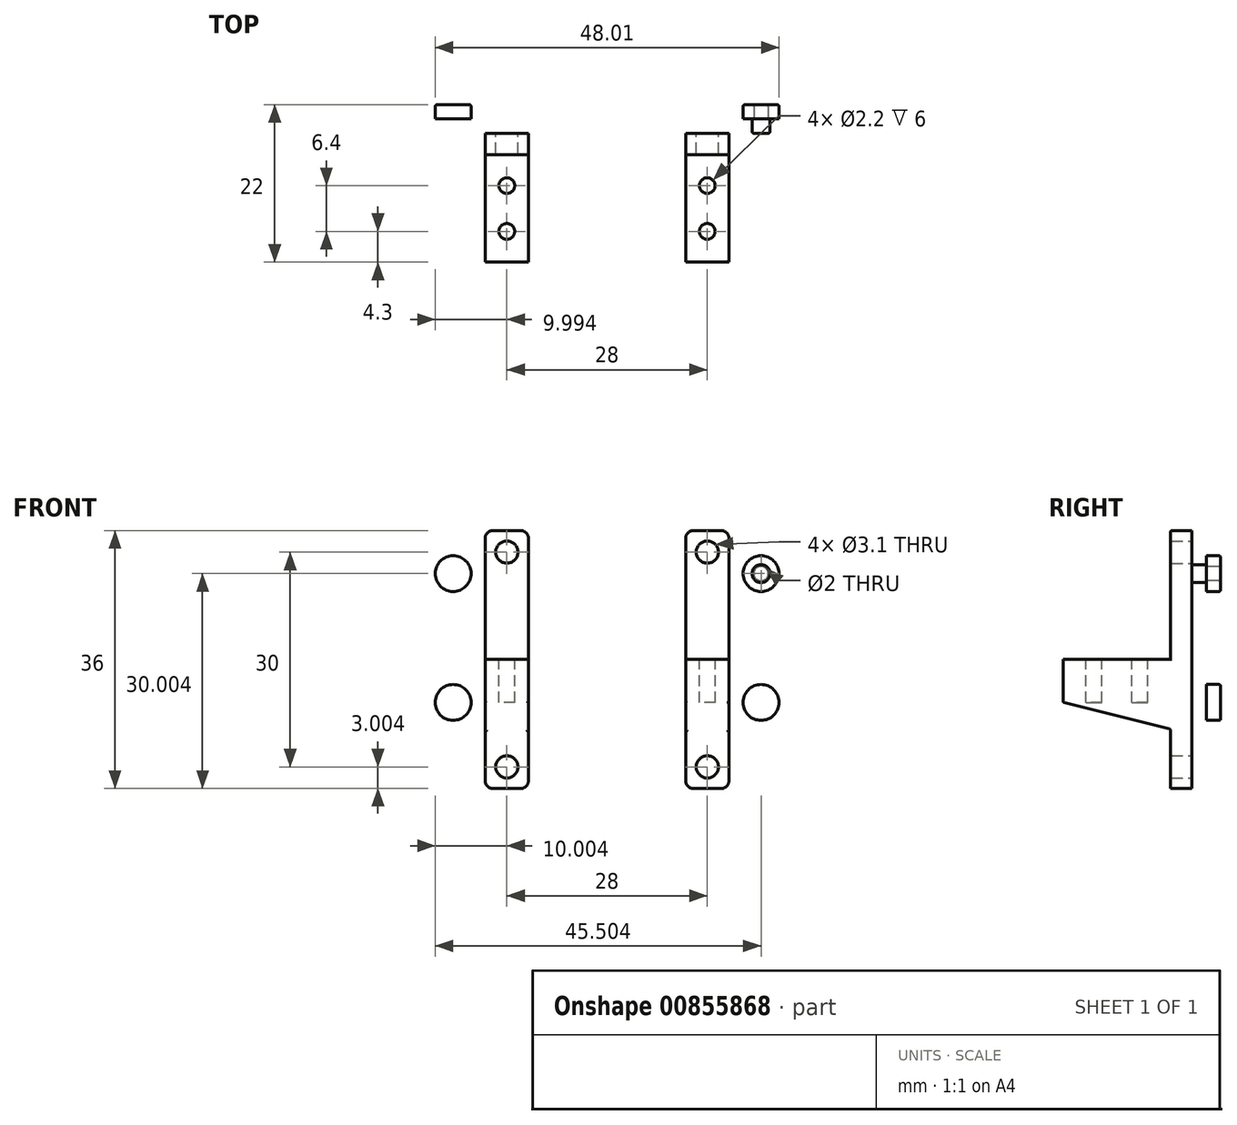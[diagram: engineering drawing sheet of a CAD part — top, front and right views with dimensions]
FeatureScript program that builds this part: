
annotation { "Feature Type Name" : "Feature", "Feature Type Description" : "" }
export const myFeature = defineFeature(function(context is Context, id is Id, definition is map)
    precondition{}
    {
        {
            var Q0;
            Q0=qCreatedBy(makeId("Front.planeOp"),FACE);
            var sketch = newSketch(context, id + "F0", { "sketchPlane" : qUnion([Q0])});
            skCircle(sketch, "E0", {"center": v(21.64, 10.68) * mm, "radius": 1.25 * mm});
            skCircle(sketch, "E1", {"center": v(21.64, -7.32) * mm, "radius": 1.25 * mm});
            skCircle(sketch, "E2", {"center": v(-21.36, 10.68) * mm, "radius": 1.25 * mm});
            skCircle(sketch, "E3", {"center": v(-21.36, -7.32) * mm, "radius": 1.25 * mm});
            skLineSegment(sketch, "E4", {"start": v(-12.6, 19.9) * mm, "end": v(12.89, 19.9) * mm});
            skLineSegment(sketch, "E5", {"start": v(-24.6, 10.6) * mm, "end": v(-24.6, -7.4) * mm});
            skLineSegment(sketch, "E6", {"start": v(24.9, 10.6) * mm, "end": v(24.9, -7.4) * mm});
            skLineSegment(sketch, "E7", {"start": v(14.2, -19.34) * mm, "end": v(-13.9, -19.34) * mm});
            skLineSegment(sketch, "E8", {"start": v(-15.36, -13.32) * mm, "end": v(-15.36, -16.32) * mm});
            skLineSegment(sketch, "E9", {"start": v(-12.36, -16.32) * mm, "end": v(-12.36, -13.32) * mm});
            skArc(sketch, "E10", {"start": v(-15.36, -16.32) * mm, "mid": v(-13.86, -17.82) * mm, "end": v(-12.36, -16.32) * mm});
            skArc(sketch, "E11", {"start": v(-12.36, -13.32) * mm, "mid": v(-13.86, -11.82) * mm, "end": v(-15.36, -13.32) * mm});
            skLineSegment(sketch, "E12", {"start": v(-15.36, 16.68) * mm, "end": v(-15.36, 13.68) * mm});
            skLineSegment(sketch, "E13", {"start": v(-12.36, 13.68) * mm, "end": v(-12.36, 16.68) * mm});
            skArc(sketch, "E14", {"start": v(-15.36, 13.68) * mm, "mid": v(-13.86, 12.18) * mm, "end": v(-12.36, 13.68) * mm});
            skArc(sketch, "E15", {"start": v(-12.36, 16.68) * mm, "mid": v(-13.86, 18.18) * mm, "end": v(-15.36, 16.68) * mm});
            skLineSegment(sketch, "E16", {"start": v(12.64, 16.68) * mm, "end": v(12.64, 13.68) * mm});
            skLineSegment(sketch, "E17", {"start": v(15.64, 13.68) * mm, "end": v(15.64, 16.68) * mm});
            skArc(sketch, "E18", {"start": v(12.64, 13.68) * mm, "mid": v(14.14, 12.18) * mm, "end": v(15.64, 13.68) * mm});
            skArc(sketch, "E19", {"start": v(15.64, 16.68) * mm, "mid": v(14.14, 18.18) * mm, "end": v(12.64, 16.68) * mm});
            skLineSegment(sketch, "E20", {"start": v(12.64, -13.32) * mm, "end": v(12.64, -16.32) * mm});
            skLineSegment(sketch, "E21", {"start": v(15.64, -16.32) * mm, "end": v(15.64, -13.32) * mm});
            skArc(sketch, "E22", {"start": v(12.64, -16.32) * mm, "mid": v(14.14, -17.82) * mm, "end": v(15.64, -16.32) * mm});
            skArc(sketch, "E23", {"start": v(15.64, -13.32) * mm, "mid": v(14.14, -11.82) * mm, "end": v(12.64, -13.32) * mm});
            skLineSegment(sketch, "E24", {"start": v(-9.86, 7.68) * mm, "end": v(-9.86, -7.32) * mm});
            skLineSegment(sketch, "E25", {"start": v(-6.86, -10.32) * mm, "end": v(7.14, -10.32) * mm});
            skLineSegment(sketch, "E26", {"start": v(10.14, -7.32) * mm, "end": v(10.14, 7.68) * mm});
            skLineSegment(sketch, "E27", {"start": v(7.14, 10.68) * mm, "end": v(-6.86, 10.68) * mm});
            skArc(sketch, "E28.filletArc", {"start": v(-6.86, 10.68) * mm, "mid": v(-8.98, 9.8) * mm, "end": v(-9.86, 7.68) * mm});
            skArc(sketch, "E29.filletArc", {"start": v(10.14, 7.68) * mm, "mid": v(9.26, 9.8) * mm, "end": v(7.14, 10.68) * mm});
            skArc(sketch, "E30.filletArc", {"start": v(7.14, -10.32) * mm, "mid": v(9.26, -9.44) * mm, "end": v(10.14, -7.32) * mm});
            skArc(sketch, "E31.filletArc", {"start": v(-9.86, -7.32) * mm, "mid": v(-8.98, -9.44) * mm, "end": v(-6.86, -10.32) * mm});
            skArc(sketch, "E32.filletArc", {"start": v(-12.6, 19.9) * mm, "mid": v(-14.56, 19.57) * mm, "end": v(-16.31, 18.61) * mm});
            skArc(sketch, "E33.filletArc", {"start": v(16.6, 18.61) * mm, "mid": v(14.85, 19.57) * mm, "end": v(12.89, 19.9) * mm});
            skLineSegment(sketch, "E34", {"start": v(23.76, -10.56) * mm, "end": v(18.06, -17.5) * mm});
            skLineSegment(sketch, "E35", {"start": v(22.57, 14.83) * mm, "end": v(16.6, 18.61) * mm});
            skLineSegment(sketch, "E36", {"start": v(-23.47, -10.56) * mm, "end": v(-17.77, -17.5) * mm});
            skLineSegment(sketch, "E37", {"start": v(-22.28, 14.83) * mm, "end": v(-16.31, 18.61) * mm});
            skArc(sketch, "E38.filletArc", {"start": v(-22.28, 14.83) * mm, "mid": v(-23.99, 13.02) * mm, "end": v(-24.6, 10.6) * mm});
            skArc(sketch, "E39.filletArc", {"start": v(-24.6, -7.4) * mm, "mid": v(-24.31, -9.08) * mm, "end": v(-23.47, -10.56) * mm});
            skArc(sketch, "E40.filletArc", {"start": v(23.76, -10.56) * mm, "mid": v(24.6, -9.08) * mm, "end": v(24.9, -7.4) * mm});
            skArc(sketch, "E41.filletArc", {"start": v(24.9, 10.6) * mm, "mid": v(24.27, 13.02) * mm, "end": v(22.57, 14.83) * mm});
            skArc(sketch, "E42.filletArc", {"start": v(-17.77, -17.5) * mm, "mid": v(-16.04, -18.86) * mm, "end": v(-13.9, -19.34) * mm});
            skArc(sketch, "E43.filletArc", {"start": v(14.2, -19.34) * mm, "mid": v(16.33, -18.86) * mm, "end": v(18.06, -17.5) * mm});
            skSolve(sketch);
        }
        {
            var Q0;
            Q0=makeQuery(id+"F0.imprint","IMPRINT",FACE,{"disambiguationData":[TD([[makeQuery(id+"F0.imprint","IMPRINT",EDGE,{"derivedFrom":sQuery(id+"F0.wireOp",EDGE,"E0")}),1.0]])]});
            extrude(context, id + "F1", {"entities" : qUnion([Q0]), "endBound" : BoundingType.SYMMETRIC, "offsetDistance" : 25 * mm, "depth" : 2 * mm});
        }
        {
            var Q0;
            Q0=makeQuery(id+"F1.opExtrude","CAP_FACE",FACE,{"disambiguationData":[OSD([sQuery(id+"F0.wireOp",EDGE,"b1f0e1de-7193-468a-b55f-a6da741b84d3"),sQuery(id+"F0.wireOp",EDGE,"6537f49a-e45f-4989-940a-a7038c38fff4"),sQuery(id+"F0.wireOp",EDGE,"8788dc07-e2e4-47d1-917b-d93742f93994"),sQuery(id+"F0.wireOp",EDGE,"47e42d19-3951-40ac-b4fd-01fcafdaa09f"),sQuery(id+"F0.wireOp",EDGE,"50e5991a-f910-4297-a0f5-58b0cc2bc1d4"),sQuery(id+"F0.wireOp",EDGE,"833c6bdf-bbd0-4c9a-a248-ca72598f08ba"),sQuery(id+"F0.wireOp",EDGE,"bd7a1b35-b3c5-4d82-882c-69e7568a474c"),sQuery(id+"F0.wireOp",EDGE,"ed142891-9665-4ff3-9cbf-df6a8f694267"),sQuery(id+"F0.wireOp",EDGE,"23a40c6b-513f-4e2b-90a4-2960991b2cb5"),sQuery(id+"F0.wireOp",EDGE,"b176ce0e-36f0-4206-846a-287cc205a3f0"),sQuery(id+"F0.wireOp",EDGE,"fd2f453c-b56c-4dc5-826e-d680bcd9d531"),sQuery(id+"F0.wireOp",EDGE,"4c904b9e-ebe1-46e0-9133-f6789165a817"),sQuery(id+"F0.wireOp",EDGE,"7d301a29-2a78-4614-95a1-4e57b7e65221"),sQuery(id+"F0.wireOp",EDGE,"bb945b4e-dbfa-4606-a6d0-c193b2a083f5"),sQuery(id+"F0.wireOp",EDGE,"f4a1adec-4f2b-4cc0-960b-66cac54fa532"),sQuery(id+"F0.wireOp",EDGE,"62c7bd33-5918-4929-8abe-04f5cd03c51a"),sQuery(id+"F0.wireOp",EDGE,"ff2f2cbf-8293-4aa6-ab80-3f50b4d68cad"),sQuery(id+"F0.wireOp",EDGE,"c173fb08-37eb-45d5-abb3-169ab915dbf1"),sQuery(id+"F0.wireOp",EDGE,"3b8e2cb5-3b84-4c06-aae3-f4915deb625e"),sQuery(id+"F0.wireOp",EDGE,"4d7a7edb-dbb5-48c5-942c-85668880a151"),sQuery(id+"F0.wireOp",EDGE,"bc3c386a-a424-47c6-a6fb-62494ecd1ae2"),sQuery(id+"F0.wireOp",EDGE,"e67013cf-1ebe-4a99-9c97-0e6cbc980e63"),sQuery(id+"F0.wireOp",EDGE,"a818867e-71c0-43a4-8c8c-aa08c8f7215a"),sQuery(id+"F0.wireOp",EDGE,"b38f441d-59fa-4f63-924d-4ace32872c36"),sQuery(id+"F0.wireOp",EDGE,"816ea5cf-f9e5-4ce4-9dad-646165a54645"),sQuery(id+"F0.wireOp",EDGE,"facd8c0d-b804-4209-a28e-61043daaaeb2"),sQuery(id+"F0.wireOp",EDGE,"7b894aa8-54af-4764-99a5-ba58160ee854"),sQuery(id+"F0.wireOp",EDGE,"c65d9a3e-1ebe-4f95-b916-c5048aa1f32a"),sQuery(id+"F0.wireOp",EDGE,"8a8d933c-0f1d-4399-bc31-42f5874e0fa8"),sQuery(id+"F0.wireOp",EDGE,"5d736322-692b-4da4-8669-e5a22c50adb5"),sQuery(id+"F0.wireOp",EDGE,"abe0f840-d98d-4ca2-984c-8d9502a8e020"),sQuery(id+"F0.wireOp",EDGE,"c0335e12-add7-4a7a-9bef-f67fba7cfbac"),sQuery(id+"F0.wireOp",EDGE,"2affc33d-ac1f-4258-a0ef-0d6ff35947cf"),sQuery(id+"F0.wireOp",EDGE,"5b7d1504-a426-47d7-bc96-b206599dc827"),sQuery(id+"F0.wireOp",EDGE,"a08130f0-2d8c-49ea-a9e2-bc1175a15415"),sQuery(id+"F0.wireOp",EDGE,"5b375d67-10b6-40a0-8c18-0bca81d9af6a"),sQuery(id+"F0.wireOp",EDGE,"d0d2f69b-842c-4d9c-a6f7-bc08b85c3292")])],"isStart":false});
            var Q1;
            Q1=makeQuery(id+"F1.opExtrude","CAP_FACE",FACE,{"disambiguationData":[OSD([sQuery(id+"F0.wireOp",EDGE,"b1f0e1de-7193-468a-b55f-a6da741b84d3"),sQuery(id+"F0.wireOp",EDGE,"6537f49a-e45f-4989-940a-a7038c38fff4"),sQuery(id+"F0.wireOp",EDGE,"8788dc07-e2e4-47d1-917b-d93742f93994"),sQuery(id+"F0.wireOp",EDGE,"47e42d19-3951-40ac-b4fd-01fcafdaa09f"),sQuery(id+"F0.wireOp",EDGE,"50e5991a-f910-4297-a0f5-58b0cc2bc1d4"),sQuery(id+"F0.wireOp",EDGE,"833c6bdf-bbd0-4c9a-a248-ca72598f08ba"),sQuery(id+"F0.wireOp",EDGE,"bd7a1b35-b3c5-4d82-882c-69e7568a474c"),sQuery(id+"F0.wireOp",EDGE,"ed142891-9665-4ff3-9cbf-df6a8f694267"),sQuery(id+"F0.wireOp",EDGE,"23a40c6b-513f-4e2b-90a4-2960991b2cb5"),sQuery(id+"F0.wireOp",EDGE,"b176ce0e-36f0-4206-846a-287cc205a3f0"),sQuery(id+"F0.wireOp",EDGE,"fd2f453c-b56c-4dc5-826e-d680bcd9d531"),sQuery(id+"F0.wireOp",EDGE,"4c904b9e-ebe1-46e0-9133-f6789165a817"),sQuery(id+"F0.wireOp",EDGE,"7d301a29-2a78-4614-95a1-4e57b7e65221"),sQuery(id+"F0.wireOp",EDGE,"bb945b4e-dbfa-4606-a6d0-c193b2a083f5"),sQuery(id+"F0.wireOp",EDGE,"f4a1adec-4f2b-4cc0-960b-66cac54fa532"),sQuery(id+"F0.wireOp",EDGE,"62c7bd33-5918-4929-8abe-04f5cd03c51a"),sQuery(id+"F0.wireOp",EDGE,"ff2f2cbf-8293-4aa6-ab80-3f50b4d68cad"),sQuery(id+"F0.wireOp",EDGE,"c173fb08-37eb-45d5-abb3-169ab915dbf1"),sQuery(id+"F0.wireOp",EDGE,"3b8e2cb5-3b84-4c06-aae3-f4915deb625e"),sQuery(id+"F0.wireOp",EDGE,"4d7a7edb-dbb5-48c5-942c-85668880a151"),sQuery(id+"F0.wireOp",EDGE,"bc3c386a-a424-47c6-a6fb-62494ecd1ae2"),sQuery(id+"F0.wireOp",EDGE,"e67013cf-1ebe-4a99-9c97-0e6cbc980e63"),sQuery(id+"F0.wireOp",EDGE,"a818867e-71c0-43a4-8c8c-aa08c8f7215a"),sQuery(id+"F0.wireOp",EDGE,"b38f441d-59fa-4f63-924d-4ace32872c36"),sQuery(id+"F0.wireOp",EDGE,"816ea5cf-f9e5-4ce4-9dad-646165a54645"),sQuery(id+"F0.wireOp",EDGE,"facd8c0d-b804-4209-a28e-61043daaaeb2"),sQuery(id+"F0.wireOp",EDGE,"7b894aa8-54af-4764-99a5-ba58160ee854"),sQuery(id+"F0.wireOp",EDGE,"c65d9a3e-1ebe-4f95-b916-c5048aa1f32a"),sQuery(id+"F0.wireOp",EDGE,"8a8d933c-0f1d-4399-bc31-42f5874e0fa8"),sQuery(id+"F0.wireOp",EDGE,"5d736322-692b-4da4-8669-e5a22c50adb5"),sQuery(id+"F0.wireOp",EDGE,"abe0f840-d98d-4ca2-984c-8d9502a8e020"),sQuery(id+"F0.wireOp",EDGE,"c0335e12-add7-4a7a-9bef-f67fba7cfbac"),sQuery(id+"F0.wireOp",EDGE,"2affc33d-ac1f-4258-a0ef-0d6ff35947cf"),sQuery(id+"F0.wireOp",EDGE,"5b7d1504-a426-47d7-bc96-b206599dc827"),sQuery(id+"F0.wireOp",EDGE,"a08130f0-2d8c-49ea-a9e2-bc1175a15415"),sQuery(id+"F0.wireOp",EDGE,"5b375d67-10b6-40a0-8c18-0bca81d9af6a"),sQuery(id+"F0.wireOp",EDGE,"d0d2f69b-842c-4d9c-a6f7-bc08b85c3292")])],"isStart":true});
            var Q2;
            Q2=makeQuery(id+"F1.opExtrude","CAP_FACE",FACE,{"disambiguationData":[OSD([sQuery(id+"F0.wireOp",EDGE,"E0"),sQuery(id+"F0.wireOp",EDGE,"E1"),sQuery(id+"F0.wireOp",EDGE,"E2"),sQuery(id+"F0.wireOp",EDGE,"E3"),sQuery(id+"F0.wireOp",EDGE,"E4"),sQuery(id+"F0.wireOp",EDGE,"E5"),sQuery(id+"F0.wireOp",EDGE,"E6"),sQuery(id+"F0.wireOp",EDGE,"E7"),sQuery(id+"F0.wireOp",EDGE,"09f95590-a519-4db1-9d27-049386f232f7"),sQuery(id+"F0.wireOp",EDGE,"f3cca56a-3ab6-4a5e-b39e-e565b3f948f0"),sQuery(id+"F0.wireOp",EDGE,"a324fc43-21dc-44d0-a907-9f37ddb06057"),sQuery(id+"F0.wireOp",EDGE,"93e36ddf-295e-42a7-bac3-406325d40537"),sQuery(id+"F0.wireOp",EDGE,"0b129f2a-8a2e-4424-b785-1e3f5dbae95f"),sQuery(id+"F0.wireOp",EDGE,"17391ced-0a03-4e9b-8a37-2fe6a2c5875e"),sQuery(id+"F0.wireOp",EDGE,"8cf102dd-5283-4df7-8a43-7ccdc88be0cf"),sQuery(id+"F0.wireOp",EDGE,"70acd655-f084-4a33-8522-e53bc09d701d"),sQuery(id+"F0.wireOp",EDGE,"f2925710-55c3-4676-86a3-d85955e98734"),sQuery(id+"F0.wireOp",EDGE,"193d501e-afe3-482a-9cb6-8f6ea38a753f"),sQuery(id+"F0.wireOp",EDGE,"8667af6c-836e-44be-96eb-cb88dcf710a9"),sQuery(id+"F0.wireOp",EDGE,"5e3e0479-6207-477d-9516-d8328ea940bd"),sQuery(id+"F0.wireOp",EDGE,"9f5e035f-f6a5-44e4-91c8-a016ac8de3eb"),sQuery(id+"F0.wireOp",EDGE,"E8"),sQuery(id+"F0.wireOp",EDGE,"E9"),sQuery(id+"F0.wireOp",EDGE,"E10"),sQuery(id+"F0.wireOp",EDGE,"E11"),sQuery(id+"F0.wireOp",EDGE,"E12"),sQuery(id+"F0.wireOp",EDGE,"E13"),sQuery(id+"F0.wireOp",EDGE,"E14"),sQuery(id+"F0.wireOp",EDGE,"E15"),sQuery(id+"F0.wireOp",EDGE,"E16"),sQuery(id+"F0.wireOp",EDGE,"E17"),sQuery(id+"F0.wireOp",EDGE,"E18"),sQuery(id+"F0.wireOp",EDGE,"E19"),sQuery(id+"F0.wireOp",EDGE,"E20"),sQuery(id+"F0.wireOp",EDGE,"E21"),sQuery(id+"F0.wireOp",EDGE,"E22"),sQuery(id+"F0.wireOp",EDGE,"E23"),sQuery(id+"F0.wireOp",EDGE,"E24"),sQuery(id+"F0.wireOp",EDGE,"E25"),sQuery(id+"F0.wireOp",EDGE,"E26"),sQuery(id+"F0.wireOp",EDGE,"E27"),sQuery(id+"F0.wireOp",EDGE,"7806fb13-56ba-4d54-8a38-79ec39868dc2"),sQuery(id+"F0.wireOp",EDGE,"23430ce5-24f0-485a-982d-6951f8ba1cb3"),sQuery(id+"F0.wireOp",EDGE,"e361aa3b-1d09-4de2-9852-f016a7084046"),sQuery(id+"F0.wireOp",EDGE,"3cd874c0-05b7-48c2-b5ff-4c1055a05f93"),sQuery(id+"F0.wireOp",EDGE,"ebd2ca65-28b3-4523-afe8-6085c673d042")])],"isStart":false});
            fillet(context, id + "F2", {"entities" : qUnion([Q0, Q1, Q2]), "radius" : .25 * mm, "tangentPropagation" : true, "allowEdgeOverflow" : false});
        }
        {
            var Q0;
            Q0=makeQuery(id+"F1.opExtrude","CAP_FACE",FACE,{"disambiguationData":[OSD([sQuery(id+"F0.wireOp",EDGE,"E0"),sQuery(id+"F0.wireOp",EDGE,"E1"),sQuery(id+"F0.wireOp",EDGE,"E2"),sQuery(id+"F0.wireOp",EDGE,"E3"),sQuery(id+"F0.wireOp",EDGE,"E4"),sQuery(id+"F0.wireOp",EDGE,"E5"),sQuery(id+"F0.wireOp",EDGE,"E6"),sQuery(id+"F0.wireOp",EDGE,"E7"),sQuery(id+"F0.wireOp",EDGE,"09f95590-a519-4db1-9d27-049386f232f7"),sQuery(id+"F0.wireOp",EDGE,"f3cca56a-3ab6-4a5e-b39e-e565b3f948f0"),sQuery(id+"F0.wireOp",EDGE,"a324fc43-21dc-44d0-a907-9f37ddb06057"),sQuery(id+"F0.wireOp",EDGE,"93e36ddf-295e-42a7-bac3-406325d40537"),sQuery(id+"F0.wireOp",EDGE,"0b129f2a-8a2e-4424-b785-1e3f5dbae95f"),sQuery(id+"F0.wireOp",EDGE,"17391ced-0a03-4e9b-8a37-2fe6a2c5875e"),sQuery(id+"F0.wireOp",EDGE,"8cf102dd-5283-4df7-8a43-7ccdc88be0cf"),sQuery(id+"F0.wireOp",EDGE,"70acd655-f084-4a33-8522-e53bc09d701d"),sQuery(id+"F0.wireOp",EDGE,"f2925710-55c3-4676-86a3-d85955e98734"),sQuery(id+"F0.wireOp",EDGE,"193d501e-afe3-482a-9cb6-8f6ea38a753f"),sQuery(id+"F0.wireOp",EDGE,"8667af6c-836e-44be-96eb-cb88dcf710a9"),sQuery(id+"F0.wireOp",EDGE,"5e3e0479-6207-477d-9516-d8328ea940bd"),sQuery(id+"F0.wireOp",EDGE,"9f5e035f-f6a5-44e4-91c8-a016ac8de3eb"),sQuery(id+"F0.wireOp",EDGE,"E8"),sQuery(id+"F0.wireOp",EDGE,"E9"),sQuery(id+"F0.wireOp",EDGE,"E10"),sQuery(id+"F0.wireOp",EDGE,"E11"),sQuery(id+"F0.wireOp",EDGE,"E12"),sQuery(id+"F0.wireOp",EDGE,"E13"),sQuery(id+"F0.wireOp",EDGE,"E14"),sQuery(id+"F0.wireOp",EDGE,"E15"),sQuery(id+"F0.wireOp",EDGE,"E16"),sQuery(id+"F0.wireOp",EDGE,"E17"),sQuery(id+"F0.wireOp",EDGE,"E18"),sQuery(id+"F0.wireOp",EDGE,"E19"),sQuery(id+"F0.wireOp",EDGE,"E20"),sQuery(id+"F0.wireOp",EDGE,"E21"),sQuery(id+"F0.wireOp",EDGE,"E22"),sQuery(id+"F0.wireOp",EDGE,"E23"),sQuery(id+"F0.wireOp",EDGE,"E24"),sQuery(id+"F0.wireOp",EDGE,"E25"),sQuery(id+"F0.wireOp",EDGE,"E26"),sQuery(id+"F0.wireOp",EDGE,"E27"),sQuery(id+"F0.wireOp",EDGE,"7806fb13-56ba-4d54-8a38-79ec39868dc2"),sQuery(id+"F0.wireOp",EDGE,"23430ce5-24f0-485a-982d-6951f8ba1cb3"),sQuery(id+"F0.wireOp",EDGE,"e361aa3b-1d09-4de2-9852-f016a7084046"),sQuery(id+"F0.wireOp",EDGE,"3cd874c0-05b7-48c2-b5ff-4c1055a05f93"),sQuery(id+"F0.wireOp",EDGE,"ebd2ca65-28b3-4523-afe8-6085c673d042")])],"isStart":true});
            fillet(context, id + "F3", {"entities" : qUnion([Q0]), "radius" : .25 * mm, "tangentPropagation" : true, "allowEdgeOverflow" : false});
        }
        {
            var Q0;
            Q0=makeQuery(id+"F1.opExtrude","CAP_FACE",FACE,{"disambiguationData":[OSD([sQuery(id+"F0.wireOp",EDGE,"E0"),sQuery(id+"F0.wireOp",EDGE,"E1"),sQuery(id+"F0.wireOp",EDGE,"E2"),sQuery(id+"F0.wireOp",EDGE,"E3"),sQuery(id+"F0.wireOp",EDGE,"E4"),sQuery(id+"F0.wireOp",EDGE,"E5"),sQuery(id+"F0.wireOp",EDGE,"E6"),sQuery(id+"F0.wireOp",EDGE,"E7"),sQuery(id+"F0.wireOp",EDGE,"09f95590-a519-4db1-9d27-049386f232f7"),sQuery(id+"F0.wireOp",EDGE,"f3cca56a-3ab6-4a5e-b39e-e565b3f948f0"),sQuery(id+"F0.wireOp",EDGE,"a324fc43-21dc-44d0-a907-9f37ddb06057"),sQuery(id+"F0.wireOp",EDGE,"93e36ddf-295e-42a7-bac3-406325d40537"),sQuery(id+"F0.wireOp",EDGE,"0b129f2a-8a2e-4424-b785-1e3f5dbae95f"),sQuery(id+"F0.wireOp",EDGE,"17391ced-0a03-4e9b-8a37-2fe6a2c5875e"),sQuery(id+"F0.wireOp",EDGE,"8cf102dd-5283-4df7-8a43-7ccdc88be0cf"),sQuery(id+"F0.wireOp",EDGE,"70acd655-f084-4a33-8522-e53bc09d701d"),sQuery(id+"F0.wireOp",EDGE,"f2925710-55c3-4676-86a3-d85955e98734"),sQuery(id+"F0.wireOp",EDGE,"193d501e-afe3-482a-9cb6-8f6ea38a753f"),sQuery(id+"F0.wireOp",EDGE,"8667af6c-836e-44be-96eb-cb88dcf710a9"),sQuery(id+"F0.wireOp",EDGE,"5e3e0479-6207-477d-9516-d8328ea940bd"),sQuery(id+"F0.wireOp",EDGE,"9f5e035f-f6a5-44e4-91c8-a016ac8de3eb"),sQuery(id+"F0.wireOp",EDGE,"E8"),sQuery(id+"F0.wireOp",EDGE,"E9"),sQuery(id+"F0.wireOp",EDGE,"E10"),sQuery(id+"F0.wireOp",EDGE,"E11"),sQuery(id+"F0.wireOp",EDGE,"E12"),sQuery(id+"F0.wireOp",EDGE,"E13"),sQuery(id+"F0.wireOp",EDGE,"E14"),sQuery(id+"F0.wireOp",EDGE,"E15"),sQuery(id+"F0.wireOp",EDGE,"E16"),sQuery(id+"F0.wireOp",EDGE,"E17"),sQuery(id+"F0.wireOp",EDGE,"E18"),sQuery(id+"F0.wireOp",EDGE,"E19"),sQuery(id+"F0.wireOp",EDGE,"E20"),sQuery(id+"F0.wireOp",EDGE,"E21"),sQuery(id+"F0.wireOp",EDGE,"E22"),sQuery(id+"F0.wireOp",EDGE,"E23"),sQuery(id+"F0.wireOp",EDGE,"E24"),sQuery(id+"F0.wireOp",EDGE,"E25"),sQuery(id+"F0.wireOp",EDGE,"E26"),sQuery(id+"F0.wireOp",EDGE,"E27"),sQuery(id+"F0.wireOp",EDGE,"7806fb13-56ba-4d54-8a38-79ec39868dc2"),sQuery(id+"F0.wireOp",EDGE,"E28.filletArc"),sQuery(id+"F0.wireOp",EDGE,"E29.filletArc"),sQuery(id+"F0.wireOp",EDGE,"E30.filletArc"),sQuery(id+"F0.wireOp",EDGE,"E31.filletArc")])],"isStart":true});
            var sketch = newSketch(context, id + "F4", { "sketchPlane" : qUnion([Q0])});
            skCircle(sketch, "E44", {"center": v(-21.64, 10.68) * mm, "radius": 2.5 * mm});
            skCircle(sketch, "E45", {"center": v(-21.64, -7.32) * mm, "radius": 2.5 * mm});
            skCircle(sketch, "E46", {"center": v(21.36, -7.32) * mm, "radius": 2.5 * mm});
            skCircle(sketch, "E47", {"center": v(21.36, 10.68) * mm, "radius": 2.5 * mm});
            skSolve(sketch);
        }
        {
            var Q0;
            Q0=makeQuery(id+"F4.imprint","IMPRINT",FACE,{"disambiguationData":[TD([[makeQuery(id+"F4.imprint","IMPRINT",EDGE,{"derivedFrom":sQuery(id+"F4.wireOp",EDGE,"E44")}),1.0]])]});
            var Q1;
            Q1=makeQuery(id+"F4.imprint","IMPRINT",FACE,{"disambiguationData":[TD([[makeQuery(id+"F4.imprint","IMPRINT",EDGE,{"derivedFrom":sQuery(id+"F4.wireOp",EDGE,"E45")}),1.0]])]});
            var Q2;
            Q2=makeQuery(id+"F4.imprint","IMPRINT",FACE,{"disambiguationData":[TD([[makeQuery(id+"F4.imprint","IMPRINT",EDGE,{"derivedFrom":sQuery(id+"F4.wireOp",EDGE,"E46")}),1.0]])]});
            var Q3;
            Q3=makeQuery(id+"F4.imprint","IMPRINT",FACE,{"disambiguationData":[TD([[makeQuery(id+"F4.imprint","IMPRINT",EDGE,{"derivedFrom":sQuery(id+"F4.wireOp",EDGE,"E47")}),1.0]])]});
            var Q4;
            Q4=sQuery(id+"F4.wireOp",EDGE,"E44");
            var Q5;
            Q5=sQuery(id+"F4.wireOp",EDGE,"E45");
            var Q6;
            Q6=sQuery(id+"F4.wireOp",EDGE,"E46");
            var Q7;
            Q7=sQuery(id+"F4.wireOp",EDGE,"E47");
            var Q8;
            Q8=sQuery(id+"F0.wireOp",EDGE,"E0");
            var Q9;
            Q9=sQuery(id+"F0.wireOp",EDGE,"E1");
            var Q10;
            Q10=sQuery(id+"F0.wireOp",EDGE,"E3");
            var Q11;
            Q11=sQuery(id+"F0.wireOp",EDGE,"E2");
            extrude(context, id + "F5", {"entities" : qUnion([Q0, Q1, Q2, Q3]), "operationType" : NewBodyOperationType.ADD, "surfaceOperationType" : NewSurfaceOperationType.ADD, "surfaceEntities" : qUnion([Q4, Q5, Q6, Q7, Q8, Q9, Q10, Q11]), "depth" : 2 * mm, "offsetDistance" : 25 * mm});
        }
        {
            var Q0;
            Q0=makeQuery(id+"F5.opExtrude","CAP_EDGE",EDGE,{"disambiguationData":[OSD([sQuery(id+"F4.wireOp",EDGE,"E47")])],"isStart":false});
            var Q1;
            {var subQ0=sQuery(id+"F0.wireOp",EDGE,"E31.filletArc");var subQ1=sQuery(id+"F0.wireOp",EDGE,"E30.filletArc");var subQ2=sQuery(id+"F0.wireOp",EDGE,"E29.filletArc");var subQ3=sQuery(id+"F0.wireOp",EDGE,"E28.filletArc");var subQ4=sQuery(id+"F0.wireOp",EDGE,"7806fb13-56ba-4d54-8a38-79ec39868dc2");var subQ5=sQuery(id+"F0.wireOp",EDGE,"E27");var subQ6=sQuery(id+"F0.wireOp",EDGE,"E26");var subQ7=sQuery(id+"F0.wireOp",EDGE,"E25");var subQ8=sQuery(id+"F0.wireOp",EDGE,"E24");var subQ9=sQuery(id+"F0.wireOp",EDGE,"E23");var subQ10=sQuery(id+"F0.wireOp",EDGE,"E22");var subQ11=sQuery(id+"F0.wireOp",EDGE,"E21");var subQ12=sQuery(id+"F0.wireOp",EDGE,"E20");var subQ13=sQuery(id+"F0.wireOp",EDGE,"E19");var subQ14=sQuery(id+"F0.wireOp",EDGE,"E18");var subQ15=sQuery(id+"F0.wireOp",EDGE,"E17");var subQ16=sQuery(id+"F0.wireOp",EDGE,"E16");var subQ17=sQuery(id+"F0.wireOp",EDGE,"E15");var subQ18=sQuery(id+"F0.wireOp",EDGE,"E14");var subQ19=sQuery(id+"F0.wireOp",EDGE,"E13");var subQ20=sQuery(id+"F0.wireOp",EDGE,"E12");var subQ21=sQuery(id+"F0.wireOp",EDGE,"E11");var subQ22=sQuery(id+"F0.wireOp",EDGE,"E10");var subQ23=sQuery(id+"F0.wireOp",EDGE,"E9");var subQ24=sQuery(id+"F0.wireOp",EDGE,"E8");var subQ25=sQuery(id+"F0.wireOp",EDGE,"9f5e035f-f6a5-44e4-91c8-a016ac8de3eb");var subQ26=sQuery(id+"F0.wireOp",EDGE,"5e3e0479-6207-477d-9516-d8328ea940bd");var subQ27=sQuery(id+"F0.wireOp",EDGE,"8667af6c-836e-44be-96eb-cb88dcf710a9");var subQ28=sQuery(id+"F0.wireOp",EDGE,"193d501e-afe3-482a-9cb6-8f6ea38a753f");var subQ29=sQuery(id+"F0.wireOp",EDGE,"f2925710-55c3-4676-86a3-d85955e98734");var subQ30=sQuery(id+"F0.wireOp",EDGE,"70acd655-f084-4a33-8522-e53bc09d701d");var subQ31=sQuery(id+"F0.wireOp",EDGE,"8cf102dd-5283-4df7-8a43-7ccdc88be0cf");var subQ32=sQuery(id+"F0.wireOp",EDGE,"17391ced-0a03-4e9b-8a37-2fe6a2c5875e");var subQ33=sQuery(id+"F0.wireOp",EDGE,"0b129f2a-8a2e-4424-b785-1e3f5dbae95f");var subQ34=sQuery(id+"F0.wireOp",EDGE,"93e36ddf-295e-42a7-bac3-406325d40537");var subQ35=sQuery(id+"F0.wireOp",EDGE,"a324fc43-21dc-44d0-a907-9f37ddb06057");var subQ36=sQuery(id+"F0.wireOp",EDGE,"f3cca56a-3ab6-4a5e-b39e-e565b3f948f0");var subQ37=sQuery(id+"F0.wireOp",EDGE,"09f95590-a519-4db1-9d27-049386f232f7");var subQ38=sQuery(id+"F0.wireOp",EDGE,"E7");var subQ39=sQuery(id+"F0.wireOp",EDGE,"E6");var subQ40=sQuery(id+"F0.wireOp",EDGE,"E5");var subQ41=sQuery(id+"F0.wireOp",EDGE,"E4");var subQ42=sQuery(id+"F0.wireOp",EDGE,"E3");var subQ43=sQuery(id+"F0.wireOp",EDGE,"E2");var subQ44=sQuery(id+"F0.wireOp",EDGE,"E1");var subQ45=sQuery(id+"F0.wireOp",EDGE,"E0");Q1=makeQuery(id+"F5.opExtrude","CAP_EDGE",EDGE,{"disambiguationData":[OSD([subQ45,subQ44,subQ43,subQ42,subQ41,subQ40,subQ39,subQ38,subQ37,subQ36,subQ35,subQ34,subQ33,subQ32,subQ31,subQ30,subQ29,subQ28,subQ27,subQ26,subQ25,subQ24,subQ23,subQ22,subQ21,subQ20,subQ19,subQ18,subQ17,subQ16,subQ15,subQ14,subQ13,subQ12,subQ11,subQ10,subQ9,subQ8,subQ7,subQ6,subQ5,subQ4,subQ3,subQ2,subQ1,subQ0]),TDD([makeQuery(id+"F4.imprint","IMPRINT",EDGE,{"derivedFrom":makeQuery(id+"F3.opFillet","BLEND_EDGE",EDGE,{"blendedFrom":[makeQuery(id+"F1.opExtrude","CAP_EDGE",EDGE,{"disambiguationData":[OSD([subQ43])],"isStart":true}),makeQuery(id+"F1.opExtrude","CAP_FACE",FACE,{"disambiguationData":[OSD([subQ45,subQ44,subQ43,subQ42,subQ41,subQ40,subQ39,subQ38,subQ37,subQ36,subQ35,subQ34,subQ33,subQ32,subQ31,subQ30,subQ29,subQ28,subQ27,subQ26,subQ25,subQ24,subQ23,subQ22,subQ21,subQ20,subQ19,subQ18,subQ17,subQ16,subQ15,subQ14,subQ13,subQ12,subQ11,subQ10,subQ9,subQ8,subQ7,subQ6,subQ5,subQ4,subQ3,subQ2,subQ1,subQ0])],"isStart":true})],"blendedInto":[makeQuery(id+"F1.opExtrude","CAP_FACE",FACE,{"disambiguationData":[OSD([subQ45,subQ44,subQ43,subQ42,subQ41,subQ40,subQ39,subQ38,subQ37,subQ36,subQ35,subQ34,subQ33,subQ32,subQ31,subQ30,subQ29,subQ28,subQ27,subQ26,subQ25,subQ24,subQ23,subQ22,subQ21,subQ20,subQ19,subQ18,subQ17,subQ16,subQ15,subQ14,subQ13,subQ12,subQ11,subQ10,subQ9,subQ8,subQ7,subQ6,subQ5,subQ4,subQ3,subQ2,subQ1,subQ0])],"isStart":true})]})})])],"isStart":false});}
            var Q2;
            Q2=makeQuery(id+"F5.opExtrude","CAP_EDGE",EDGE,{"disambiguationData":[OSD([sQuery(id+"F4.wireOp",EDGE,"E44")])],"isStart":false});
            var Q3;
            {var subQ0=sQuery(id+"F0.wireOp",EDGE,"E31.filletArc");var subQ1=sQuery(id+"F0.wireOp",EDGE,"E30.filletArc");var subQ2=sQuery(id+"F0.wireOp",EDGE,"E29.filletArc");var subQ3=sQuery(id+"F0.wireOp",EDGE,"E28.filletArc");var subQ4=sQuery(id+"F0.wireOp",EDGE,"7806fb13-56ba-4d54-8a38-79ec39868dc2");var subQ5=sQuery(id+"F0.wireOp",EDGE,"E27");var subQ6=sQuery(id+"F0.wireOp",EDGE,"E26");var subQ7=sQuery(id+"F0.wireOp",EDGE,"E25");var subQ8=sQuery(id+"F0.wireOp",EDGE,"E24");var subQ9=sQuery(id+"F0.wireOp",EDGE,"E23");var subQ10=sQuery(id+"F0.wireOp",EDGE,"E22");var subQ11=sQuery(id+"F0.wireOp",EDGE,"E21");var subQ12=sQuery(id+"F0.wireOp",EDGE,"E20");var subQ13=sQuery(id+"F0.wireOp",EDGE,"E19");var subQ14=sQuery(id+"F0.wireOp",EDGE,"E18");var subQ15=sQuery(id+"F0.wireOp",EDGE,"E17");var subQ16=sQuery(id+"F0.wireOp",EDGE,"E16");var subQ17=sQuery(id+"F0.wireOp",EDGE,"E15");var subQ18=sQuery(id+"F0.wireOp",EDGE,"E14");var subQ19=sQuery(id+"F0.wireOp",EDGE,"E13");var subQ20=sQuery(id+"F0.wireOp",EDGE,"E12");var subQ21=sQuery(id+"F0.wireOp",EDGE,"E11");var subQ22=sQuery(id+"F0.wireOp",EDGE,"E10");var subQ23=sQuery(id+"F0.wireOp",EDGE,"E9");var subQ24=sQuery(id+"F0.wireOp",EDGE,"E8");var subQ25=sQuery(id+"F0.wireOp",EDGE,"9f5e035f-f6a5-44e4-91c8-a016ac8de3eb");var subQ26=sQuery(id+"F0.wireOp",EDGE,"5e3e0479-6207-477d-9516-d8328ea940bd");var subQ27=sQuery(id+"F0.wireOp",EDGE,"8667af6c-836e-44be-96eb-cb88dcf710a9");var subQ28=sQuery(id+"F0.wireOp",EDGE,"193d501e-afe3-482a-9cb6-8f6ea38a753f");var subQ29=sQuery(id+"F0.wireOp",EDGE,"f2925710-55c3-4676-86a3-d85955e98734");var subQ30=sQuery(id+"F0.wireOp",EDGE,"70acd655-f084-4a33-8522-e53bc09d701d");var subQ31=sQuery(id+"F0.wireOp",EDGE,"8cf102dd-5283-4df7-8a43-7ccdc88be0cf");var subQ32=sQuery(id+"F0.wireOp",EDGE,"17391ced-0a03-4e9b-8a37-2fe6a2c5875e");var subQ33=sQuery(id+"F0.wireOp",EDGE,"0b129f2a-8a2e-4424-b785-1e3f5dbae95f");var subQ34=sQuery(id+"F0.wireOp",EDGE,"93e36ddf-295e-42a7-bac3-406325d40537");var subQ35=sQuery(id+"F0.wireOp",EDGE,"a324fc43-21dc-44d0-a907-9f37ddb06057");var subQ36=sQuery(id+"F0.wireOp",EDGE,"f3cca56a-3ab6-4a5e-b39e-e565b3f948f0");var subQ37=sQuery(id+"F0.wireOp",EDGE,"09f95590-a519-4db1-9d27-049386f232f7");var subQ38=sQuery(id+"F0.wireOp",EDGE,"E7");var subQ39=sQuery(id+"F0.wireOp",EDGE,"E6");var subQ40=sQuery(id+"F0.wireOp",EDGE,"E5");var subQ41=sQuery(id+"F0.wireOp",EDGE,"E4");var subQ42=sQuery(id+"F0.wireOp",EDGE,"E3");var subQ43=sQuery(id+"F0.wireOp",EDGE,"E2");var subQ44=sQuery(id+"F0.wireOp",EDGE,"E1");var subQ45=sQuery(id+"F0.wireOp",EDGE,"E0");Q3=makeQuery(id+"F5.opExtrude","CAP_EDGE",EDGE,{"disambiguationData":[OSD([subQ45,subQ44,subQ43,subQ42,subQ41,subQ40,subQ39,subQ38,subQ37,subQ36,subQ35,subQ34,subQ33,subQ32,subQ31,subQ30,subQ29,subQ28,subQ27,subQ26,subQ25,subQ24,subQ23,subQ22,subQ21,subQ20,subQ19,subQ18,subQ17,subQ16,subQ15,subQ14,subQ13,subQ12,subQ11,subQ10,subQ9,subQ8,subQ7,subQ6,subQ5,subQ4,subQ3,subQ2,subQ1,subQ0]),TDD([makeQuery(id+"F4.imprint","IMPRINT",EDGE,{"derivedFrom":makeQuery(id+"F3.opFillet","BLEND_EDGE",EDGE,{"blendedFrom":[makeQuery(id+"F1.opExtrude","CAP_EDGE",EDGE,{"disambiguationData":[OSD([subQ45])],"isStart":true}),makeQuery(id+"F1.opExtrude","CAP_FACE",FACE,{"disambiguationData":[OSD([subQ45,subQ44,subQ43,subQ42,subQ41,subQ40,subQ39,subQ38,subQ37,subQ36,subQ35,subQ34,subQ33,subQ32,subQ31,subQ30,subQ29,subQ28,subQ27,subQ26,subQ25,subQ24,subQ23,subQ22,subQ21,subQ20,subQ19,subQ18,subQ17,subQ16,subQ15,subQ14,subQ13,subQ12,subQ11,subQ10,subQ9,subQ8,subQ7,subQ6,subQ5,subQ4,subQ3,subQ2,subQ1,subQ0])],"isStart":true})],"blendedInto":[makeQuery(id+"F1.opExtrude","CAP_FACE",FACE,{"disambiguationData":[OSD([subQ45,subQ44,subQ43,subQ42,subQ41,subQ40,subQ39,subQ38,subQ37,subQ36,subQ35,subQ34,subQ33,subQ32,subQ31,subQ30,subQ29,subQ28,subQ27,subQ26,subQ25,subQ24,subQ23,subQ22,subQ21,subQ20,subQ19,subQ18,subQ17,subQ16,subQ15,subQ14,subQ13,subQ12,subQ11,subQ10,subQ9,subQ8,subQ7,subQ6,subQ5,subQ4,subQ3,subQ2,subQ1,subQ0])],"isStart":true})]})})])],"isStart":false});}
            var Q4;
            Q4=makeQuery(id+"F5.opExtrude","CAP_EDGE",EDGE,{"disambiguationData":[OSD([sQuery(id+"F4.wireOp",EDGE,"E45")])],"isStart":false});
            var Q5;
            {var subQ0=sQuery(id+"F0.wireOp",EDGE,"E31.filletArc");var subQ1=sQuery(id+"F0.wireOp",EDGE,"E30.filletArc");var subQ2=sQuery(id+"F0.wireOp",EDGE,"E29.filletArc");var subQ3=sQuery(id+"F0.wireOp",EDGE,"E28.filletArc");var subQ4=sQuery(id+"F0.wireOp",EDGE,"7806fb13-56ba-4d54-8a38-79ec39868dc2");var subQ5=sQuery(id+"F0.wireOp",EDGE,"E27");var subQ6=sQuery(id+"F0.wireOp",EDGE,"E26");var subQ7=sQuery(id+"F0.wireOp",EDGE,"E25");var subQ8=sQuery(id+"F0.wireOp",EDGE,"E24");var subQ9=sQuery(id+"F0.wireOp",EDGE,"E23");var subQ10=sQuery(id+"F0.wireOp",EDGE,"E22");var subQ11=sQuery(id+"F0.wireOp",EDGE,"E21");var subQ12=sQuery(id+"F0.wireOp",EDGE,"E20");var subQ13=sQuery(id+"F0.wireOp",EDGE,"E19");var subQ14=sQuery(id+"F0.wireOp",EDGE,"E18");var subQ15=sQuery(id+"F0.wireOp",EDGE,"E17");var subQ16=sQuery(id+"F0.wireOp",EDGE,"E16");var subQ17=sQuery(id+"F0.wireOp",EDGE,"E15");var subQ18=sQuery(id+"F0.wireOp",EDGE,"E14");var subQ19=sQuery(id+"F0.wireOp",EDGE,"E13");var subQ20=sQuery(id+"F0.wireOp",EDGE,"E12");var subQ21=sQuery(id+"F0.wireOp",EDGE,"E11");var subQ22=sQuery(id+"F0.wireOp",EDGE,"E10");var subQ23=sQuery(id+"F0.wireOp",EDGE,"E9");var subQ24=sQuery(id+"F0.wireOp",EDGE,"E8");var subQ25=sQuery(id+"F0.wireOp",EDGE,"9f5e035f-f6a5-44e4-91c8-a016ac8de3eb");var subQ26=sQuery(id+"F0.wireOp",EDGE,"5e3e0479-6207-477d-9516-d8328ea940bd");var subQ27=sQuery(id+"F0.wireOp",EDGE,"8667af6c-836e-44be-96eb-cb88dcf710a9");var subQ28=sQuery(id+"F0.wireOp",EDGE,"193d501e-afe3-482a-9cb6-8f6ea38a753f");var subQ29=sQuery(id+"F0.wireOp",EDGE,"f2925710-55c3-4676-86a3-d85955e98734");var subQ30=sQuery(id+"F0.wireOp",EDGE,"70acd655-f084-4a33-8522-e53bc09d701d");var subQ31=sQuery(id+"F0.wireOp",EDGE,"8cf102dd-5283-4df7-8a43-7ccdc88be0cf");var subQ32=sQuery(id+"F0.wireOp",EDGE,"17391ced-0a03-4e9b-8a37-2fe6a2c5875e");var subQ33=sQuery(id+"F0.wireOp",EDGE,"0b129f2a-8a2e-4424-b785-1e3f5dbae95f");var subQ34=sQuery(id+"F0.wireOp",EDGE,"93e36ddf-295e-42a7-bac3-406325d40537");var subQ35=sQuery(id+"F0.wireOp",EDGE,"a324fc43-21dc-44d0-a907-9f37ddb06057");var subQ36=sQuery(id+"F0.wireOp",EDGE,"f3cca56a-3ab6-4a5e-b39e-e565b3f948f0");var subQ37=sQuery(id+"F0.wireOp",EDGE,"09f95590-a519-4db1-9d27-049386f232f7");var subQ38=sQuery(id+"F0.wireOp",EDGE,"E7");var subQ39=sQuery(id+"F0.wireOp",EDGE,"E6");var subQ40=sQuery(id+"F0.wireOp",EDGE,"E5");var subQ41=sQuery(id+"F0.wireOp",EDGE,"E4");var subQ42=sQuery(id+"F0.wireOp",EDGE,"E3");var subQ43=sQuery(id+"F0.wireOp",EDGE,"E2");var subQ44=sQuery(id+"F0.wireOp",EDGE,"E1");var subQ45=sQuery(id+"F0.wireOp",EDGE,"E0");Q5=makeQuery(id+"F5.opExtrude","CAP_EDGE",EDGE,{"disambiguationData":[OSD([subQ45,subQ44,subQ43,subQ42,subQ41,subQ40,subQ39,subQ38,subQ37,subQ36,subQ35,subQ34,subQ33,subQ32,subQ31,subQ30,subQ29,subQ28,subQ27,subQ26,subQ25,subQ24,subQ23,subQ22,subQ21,subQ20,subQ19,subQ18,subQ17,subQ16,subQ15,subQ14,subQ13,subQ12,subQ11,subQ10,subQ9,subQ8,subQ7,subQ6,subQ5,subQ4,subQ3,subQ2,subQ1,subQ0]),TDD([makeQuery(id+"F4.imprint","IMPRINT",EDGE,{"derivedFrom":makeQuery(id+"F3.opFillet","BLEND_EDGE",EDGE,{"blendedFrom":[makeQuery(id+"F1.opExtrude","CAP_EDGE",EDGE,{"disambiguationData":[OSD([subQ44])],"isStart":true}),makeQuery(id+"F1.opExtrude","CAP_FACE",FACE,{"disambiguationData":[OSD([subQ45,subQ44,subQ43,subQ42,subQ41,subQ40,subQ39,subQ38,subQ37,subQ36,subQ35,subQ34,subQ33,subQ32,subQ31,subQ30,subQ29,subQ28,subQ27,subQ26,subQ25,subQ24,subQ23,subQ22,subQ21,subQ20,subQ19,subQ18,subQ17,subQ16,subQ15,subQ14,subQ13,subQ12,subQ11,subQ10,subQ9,subQ8,subQ7,subQ6,subQ5,subQ4,subQ3,subQ2,subQ1,subQ0])],"isStart":true})],"blendedInto":[makeQuery(id+"F1.opExtrude","CAP_FACE",FACE,{"disambiguationData":[OSD([subQ45,subQ44,subQ43,subQ42,subQ41,subQ40,subQ39,subQ38,subQ37,subQ36,subQ35,subQ34,subQ33,subQ32,subQ31,subQ30,subQ29,subQ28,subQ27,subQ26,subQ25,subQ24,subQ23,subQ22,subQ21,subQ20,subQ19,subQ18,subQ17,subQ16,subQ15,subQ14,subQ13,subQ12,subQ11,subQ10,subQ9,subQ8,subQ7,subQ6,subQ5,subQ4,subQ3,subQ2,subQ1,subQ0])],"isStart":true})]})})])],"isStart":false});}
            var Q6;
            {var subQ0=sQuery(id+"F0.wireOp",EDGE,"E31.filletArc");var subQ1=sQuery(id+"F0.wireOp",EDGE,"E30.filletArc");var subQ2=sQuery(id+"F0.wireOp",EDGE,"E29.filletArc");var subQ3=sQuery(id+"F0.wireOp",EDGE,"E28.filletArc");var subQ4=sQuery(id+"F0.wireOp",EDGE,"7806fb13-56ba-4d54-8a38-79ec39868dc2");var subQ5=sQuery(id+"F0.wireOp",EDGE,"E27");var subQ6=sQuery(id+"F0.wireOp",EDGE,"E26");var subQ7=sQuery(id+"F0.wireOp",EDGE,"E25");var subQ8=sQuery(id+"F0.wireOp",EDGE,"E24");var subQ9=sQuery(id+"F0.wireOp",EDGE,"E23");var subQ10=sQuery(id+"F0.wireOp",EDGE,"E22");var subQ11=sQuery(id+"F0.wireOp",EDGE,"E21");var subQ12=sQuery(id+"F0.wireOp",EDGE,"E20");var subQ13=sQuery(id+"F0.wireOp",EDGE,"E19");var subQ14=sQuery(id+"F0.wireOp",EDGE,"E18");var subQ15=sQuery(id+"F0.wireOp",EDGE,"E17");var subQ16=sQuery(id+"F0.wireOp",EDGE,"E16");var subQ17=sQuery(id+"F0.wireOp",EDGE,"E15");var subQ18=sQuery(id+"F0.wireOp",EDGE,"E14");var subQ19=sQuery(id+"F0.wireOp",EDGE,"E13");var subQ20=sQuery(id+"F0.wireOp",EDGE,"E12");var subQ21=sQuery(id+"F0.wireOp",EDGE,"E11");var subQ22=sQuery(id+"F0.wireOp",EDGE,"E10");var subQ23=sQuery(id+"F0.wireOp",EDGE,"E9");var subQ24=sQuery(id+"F0.wireOp",EDGE,"E8");var subQ25=sQuery(id+"F0.wireOp",EDGE,"9f5e035f-f6a5-44e4-91c8-a016ac8de3eb");var subQ26=sQuery(id+"F0.wireOp",EDGE,"5e3e0479-6207-477d-9516-d8328ea940bd");var subQ27=sQuery(id+"F0.wireOp",EDGE,"8667af6c-836e-44be-96eb-cb88dcf710a9");var subQ28=sQuery(id+"F0.wireOp",EDGE,"193d501e-afe3-482a-9cb6-8f6ea38a753f");var subQ29=sQuery(id+"F0.wireOp",EDGE,"f2925710-55c3-4676-86a3-d85955e98734");var subQ30=sQuery(id+"F0.wireOp",EDGE,"70acd655-f084-4a33-8522-e53bc09d701d");var subQ31=sQuery(id+"F0.wireOp",EDGE,"8cf102dd-5283-4df7-8a43-7ccdc88be0cf");var subQ32=sQuery(id+"F0.wireOp",EDGE,"17391ced-0a03-4e9b-8a37-2fe6a2c5875e");var subQ33=sQuery(id+"F0.wireOp",EDGE,"0b129f2a-8a2e-4424-b785-1e3f5dbae95f");var subQ34=sQuery(id+"F0.wireOp",EDGE,"93e36ddf-295e-42a7-bac3-406325d40537");var subQ35=sQuery(id+"F0.wireOp",EDGE,"a324fc43-21dc-44d0-a907-9f37ddb06057");var subQ36=sQuery(id+"F0.wireOp",EDGE,"f3cca56a-3ab6-4a5e-b39e-e565b3f948f0");var subQ37=sQuery(id+"F0.wireOp",EDGE,"09f95590-a519-4db1-9d27-049386f232f7");var subQ38=sQuery(id+"F0.wireOp",EDGE,"E7");var subQ39=sQuery(id+"F0.wireOp",EDGE,"E6");var subQ40=sQuery(id+"F0.wireOp",EDGE,"E5");var subQ41=sQuery(id+"F0.wireOp",EDGE,"E4");var subQ42=sQuery(id+"F0.wireOp",EDGE,"E3");var subQ43=sQuery(id+"F0.wireOp",EDGE,"E2");var subQ44=sQuery(id+"F0.wireOp",EDGE,"E1");var subQ45=sQuery(id+"F0.wireOp",EDGE,"E0");Q6=makeQuery(id+"F5.opExtrude","CAP_EDGE",EDGE,{"disambiguationData":[OSD([subQ45,subQ44,subQ43,subQ42,subQ41,subQ40,subQ39,subQ38,subQ37,subQ36,subQ35,subQ34,subQ33,subQ32,subQ31,subQ30,subQ29,subQ28,subQ27,subQ26,subQ25,subQ24,subQ23,subQ22,subQ21,subQ20,subQ19,subQ18,subQ17,subQ16,subQ15,subQ14,subQ13,subQ12,subQ11,subQ10,subQ9,subQ8,subQ7,subQ6,subQ5,subQ4,subQ3,subQ2,subQ1,subQ0]),TDD([makeQuery(id+"F4.imprint","IMPRINT",EDGE,{"derivedFrom":makeQuery(id+"F3.opFillet","BLEND_EDGE",EDGE,{"blendedFrom":[makeQuery(id+"F1.opExtrude","CAP_EDGE",EDGE,{"disambiguationData":[OSD([subQ42])],"isStart":true}),makeQuery(id+"F1.opExtrude","CAP_FACE",FACE,{"disambiguationData":[OSD([subQ45,subQ44,subQ43,subQ42,subQ41,subQ40,subQ39,subQ38,subQ37,subQ36,subQ35,subQ34,subQ33,subQ32,subQ31,subQ30,subQ29,subQ28,subQ27,subQ26,subQ25,subQ24,subQ23,subQ22,subQ21,subQ20,subQ19,subQ18,subQ17,subQ16,subQ15,subQ14,subQ13,subQ12,subQ11,subQ10,subQ9,subQ8,subQ7,subQ6,subQ5,subQ4,subQ3,subQ2,subQ1,subQ0])],"isStart":true})],"blendedInto":[makeQuery(id+"F1.opExtrude","CAP_FACE",FACE,{"disambiguationData":[OSD([subQ45,subQ44,subQ43,subQ42,subQ41,subQ40,subQ39,subQ38,subQ37,subQ36,subQ35,subQ34,subQ33,subQ32,subQ31,subQ30,subQ29,subQ28,subQ27,subQ26,subQ25,subQ24,subQ23,subQ22,subQ21,subQ20,subQ19,subQ18,subQ17,subQ16,subQ15,subQ14,subQ13,subQ12,subQ11,subQ10,subQ9,subQ8,subQ7,subQ6,subQ5,subQ4,subQ3,subQ2,subQ1,subQ0])],"isStart":true})]})})])],"isStart":false});}
            var Q7;
            Q7=makeQuery(id+"F5.opExtrude","CAP_EDGE",EDGE,{"disambiguationData":[OSD([sQuery(id+"F4.wireOp",EDGE,"E46")])],"isStart":false});
            fillet(context, id + "F6", {"entities" : qUnion([Q0, Q1, Q2, Q3, Q4, Q5, Q6, Q7]), "radius" : .25 * mm, "tangentPropagation" : true, "allowEdgeOverflow" : false});
        }
        {
            var Q0;
            Q0=makeQuery(id+"F1.opExtrude","CAP_FACE",FACE,{"disambiguationData":[OSD([sQuery(id+"F0.wireOp",EDGE,"E0"),sQuery(id+"F0.wireOp",EDGE,"E1"),sQuery(id+"F0.wireOp",EDGE,"E2"),sQuery(id+"F0.wireOp",EDGE,"E3"),sQuery(id+"F0.wireOp",EDGE,"E4"),sQuery(id+"F0.wireOp",EDGE,"E5"),sQuery(id+"F0.wireOp",EDGE,"E6"),sQuery(id+"F0.wireOp",EDGE,"E7"),sQuery(id+"F0.wireOp",EDGE,"09f95590-a519-4db1-9d27-049386f232f7"),sQuery(id+"F0.wireOp",EDGE,"f3cca56a-3ab6-4a5e-b39e-e565b3f948f0"),sQuery(id+"F0.wireOp",EDGE,"a324fc43-21dc-44d0-a907-9f37ddb06057"),sQuery(id+"F0.wireOp",EDGE,"93e36ddf-295e-42a7-bac3-406325d40537"),sQuery(id+"F0.wireOp",EDGE,"70acd655-f084-4a33-8522-e53bc09d701d"),sQuery(id+"F0.wireOp",EDGE,"f2925710-55c3-4676-86a3-d85955e98734"),sQuery(id+"F0.wireOp",EDGE,"193d501e-afe3-482a-9cb6-8f6ea38a753f"),sQuery(id+"F0.wireOp",EDGE,"8667af6c-836e-44be-96eb-cb88dcf710a9"),sQuery(id+"F0.wireOp",EDGE,"5e3e0479-6207-477d-9516-d8328ea940bd"),sQuery(id+"F0.wireOp",EDGE,"9f5e035f-f6a5-44e4-91c8-a016ac8de3eb"),sQuery(id+"F0.wireOp",EDGE,"E8"),sQuery(id+"F0.wireOp",EDGE,"E9"),sQuery(id+"F0.wireOp",EDGE,"E10"),sQuery(id+"F0.wireOp",EDGE,"E11"),sQuery(id+"F0.wireOp",EDGE,"E12"),sQuery(id+"F0.wireOp",EDGE,"E13"),sQuery(id+"F0.wireOp",EDGE,"E14"),sQuery(id+"F0.wireOp",EDGE,"E15"),sQuery(id+"F0.wireOp",EDGE,"E16"),sQuery(id+"F0.wireOp",EDGE,"E17"),sQuery(id+"F0.wireOp",EDGE,"E18"),sQuery(id+"F0.wireOp",EDGE,"E19"),sQuery(id+"F0.wireOp",EDGE,"E20"),sQuery(id+"F0.wireOp",EDGE,"E21"),sQuery(id+"F0.wireOp",EDGE,"E22"),sQuery(id+"F0.wireOp",EDGE,"E23"),sQuery(id+"F0.wireOp",EDGE,"E24"),sQuery(id+"F0.wireOp",EDGE,"E25"),sQuery(id+"F0.wireOp",EDGE,"E26"),sQuery(id+"F0.wireOp",EDGE,"E27"),sQuery(id+"F0.wireOp",EDGE,"E28.filletArc"),sQuery(id+"F0.wireOp",EDGE,"E29.filletArc"),sQuery(id+"F0.wireOp",EDGE,"E30.filletArc"),sQuery(id+"F0.wireOp",EDGE,"E31.filletArc"),sQuery(id+"F0.wireOp",EDGE,"E32.filletArc"),sQuery(id+"F0.wireOp",EDGE,"0a8ec9ba-700e-4d73-9070-ab5185d5a21f0.MirrorCS"),sQuery(id+"F0.wireOp",EDGE,"E33.filletArc")])],"isStart":false});
            var sketch = newSketch(context, id + "F7", { "sketchPlane" : qUnion([Q0])});
            skLineSegment(sketch, "E48.bottom", {"start": v(-15.86, 16.68) * mm, "end": v(-11.86, 16.68) * mm});
            skLineSegment(sketch, "E48.top", {"start": v(-15.86, -19.32) * mm, "end": v(-11.86, -19.32) * mm});
            skLineSegment(sketch, "E48.left", {"start": v(-16.86, 15.68) * mm, "end": v(-16.86, -18.32) * mm});
            skLineSegment(sketch, "E48.right", {"start": v(-10.86, 15.68) * mm, "end": v(-10.86, -18.32) * mm});
            skCircle(sketch, "E49", {"center": v(-13.86, 13.68) * mm, "radius": 1.55 * mm});
            skPoint(sketch, "E49.centerSnap0", {"position": v(-13.86, 16.68) * mm});
            skCircle(sketch, "E50", {"center": v(-13.86, -16.32) * mm, "radius": 1.55 * mm});
            skPoint(sketch, "E51.visualSharp", {"position": v(-16.86, 16.68) * mm});
            skArc(sketch, "E51.filletArc", {"start": v(-15.86, 16.68) * mm, "mid": v(-16.56, 16.4) * mm, "end": v(-16.86, 15.68) * mm});
            skPoint(sketch, "E52.visualSharp", {"position": v(-10.86, 16.68) * mm});
            skArc(sketch, "E52.filletArc", {"start": v(-10.86, 15.68) * mm, "mid": v(-11.15, 16.4) * mm, "end": v(-11.86, 16.68) * mm});
            skPoint(sketch, "E53.visualSharp", {"position": v(-10.86, -19.32) * mm});
            skArc(sketch, "E53.filletArc", {"start": v(-11.86, -19.32) * mm, "mid": v(-11.15, -19.02) * mm, "end": v(-10.86, -18.32) * mm});
            skPoint(sketch, "E54.visualSharp", {"position": v(-16.86, -19.32) * mm});
            skArc(sketch, "E54.filletArc", {"start": v(-16.86, -18.32) * mm, "mid": v(-16.56, -19.02) * mm, "end": v(-15.86, -19.32) * mm});
            skLineSegment(sketch, "E55.bottom", {"start": v(-16.86, -1.32) * mm, "end": v(-10.86, -1.32) * mm});
            skLineSegment(sketch, "E56.top", {"start": v(-16.86, -11.32) * mm, "end": v(-10.86, -11.32) * mm});
            skLineSegment(sketch, "E56.left", {"start": v(-16.86, -1.32) * mm, "end": v(-16.86, -11.32) * mm});
            skLineSegment(sketch, "E56.right", {"start": v(-10.86, -1.32) * mm, "end": v(-10.86, -11.32) * mm});
            skSolve(sketch);
        }
        {
            var Q0;
            Q0 = qSketchRegion(id + "F7", true);
            extrude(context, id + "F8", {"entities" : qUnion([Q0]), "depth" : 3 * mm, "offsetDistance" : 25 * mm});
        }
        {
            var Q0;
            Q0=makeQuery(id+"F7.imprint","IMPRINT",FACE,{"disambiguationData":[TD([[makeQuery(id+"F7.imprint","IMPRINT",EDGE,{"derivedFrom":sQuery(id+"F7.wireOp",EDGE,"E55.bottom")}),-1.0]])]});
            extrude(context, id + "F9", {"entities" : qUnion([Q0]), "operationType" : NewBodyOperationType.ADD, "depth" : 18 * mm, "offsetDistance" : 25 * mm});
        }
        {
            var Q0;
            Q0=makeQuery(id+"F9.opExtrude","CAP_EDGE",EDGE,{"disambiguationData":[OSD([sQuery(id+"F7.wireOp",EDGE,"E56.top")])],"isStart":false});
            chamfer(context, id + "F10", {"entities" : qUnion([Q0]), "chamferType" : ChamferType.TWO_OFFSETS, "width1" : 4 * mm, "oppositeDirection" : false, "width2" : 16 * mm, "tangentPropagation" : true});
        }
        {
            var Q0;
            Q0=makeQuery(id+"F9.opExtrude","SWEPT_FACE",FACE,{"disambiguationData":[OSD([sQuery(id+"F7.wireOp",EDGE,"E55.bottom")])]});
            var sketch = newSketch(context, id + "F11", { "sketchPlane" : qUnion([Q0])});
            skCircle(sketch, "E57", {"center": v(-13.87, -8.3) * mm, "radius": 1.1 * mm});
            skPoint(sketch, "E57.centerSnap0", {"position": v(-13.87, -1) * mm});
            skCircle(sketch, "E58", {"center": v(-13.87, -14.7) * mm, "radius": 1.1 * mm});
            skPoint(sketch, "E58.centerSnap0", {"position": v(-13.87, -5.63) * mm});
            skSolve(sketch);
        }
        {
            var Q0;
            Q0 = qSketchRegion(id + "F11", true);
            extrude(context, id + "F12", {"entities" : qUnion([Q0]), "operationType" : NewBodyOperationType.REMOVE, "oppositeDirection" : true, "depth" : 6 * mm, "offsetDistance" : 25 * mm, "hasSecondDirection" : true, "secondDirectionOppositeDirection" : false, "secondDirectionDepth" : 6 * mm});
        }
        {
            var Q0;
            Q0=makeQuery(id+"F10.opChamfer","BLEND_FACE",FACE,{"disambiguationData":[OSD([sQuery(id+"F7.wireOp",EDGE,"E56.top")])]});
            var Q1;
            Q1=makeQuery(id+"F9.opExtrude","CAP_EDGE",EDGE,{"disambiguationData":[OSD([sQuery(id+"F7.wireOp",EDGE,"E56.left")])],"isStart":false});
            var Q2;
            Q2=makeQuery(id+"F9.opExtrude","CAP_EDGE",EDGE,{"disambiguationData":[OSD([sQuery(id+"F7.wireOp",EDGE,"E56.right")])],"isStart":false});
            var Q3;
            {var subQ0=sQuery(id+"F7.wireOp",EDGE,"E56.left");var subQ1=sQuery(id+"F7.wireOp",EDGE,"E48.left");var subQ2=sQuery(id+"F7.wireOp",EDGE,"E51.filletArc");Q3=makeQuery(id+"F9.boolean.opBoolean","SPLIT",EDGE,{"disambiguationData":[TD([makeQuery(id+"F8.opExtrude","SWEPT_FACE",FACE,{"disambiguationData":[OSD([subQ2])]})])],"derivedFrom":makeQuery(id+"F8.opExtrude","CAP_EDGE",EDGE,{"disambiguationData":[OSD([subQ1,subQ0])],"isStart":false})});}
            var Q4;
            Q4=makeQuery(id+"F8.opExtrude","CAP_EDGE",EDGE,{"disambiguationData":[OSD([sQuery(id+"F7.wireOp",EDGE,"E49")])],"isStart":false});
            var Q5;
            Q5=makeQuery(id+"F8.opExtrude","CAP_EDGE",EDGE,{"disambiguationData":[OSD([sQuery(id+"F7.wireOp",EDGE,"E50")])],"isStart":false});
            fillet(context, id + "F13", {"entities" : qUnion([Q0, Q1, Q2, Q3, Q4, Q5]), "radius" : .2 * mm, "tangentPropagation" : true, "allowEdgeOverflow" : false});
        }
        {
            var Q0;
            Q0=makeQuery(id+"F8.opExtrude","SWEPT_BODY",BODY,{"disambiguationData":[OSD([sQuery(id+"F7.wireOp",EDGE,"E48.bottom"),sQuery(id+"F7.wireOp",EDGE,"E48.top"),sQuery(id+"F7.wireOp",EDGE,"E48.left"),sQuery(id+"F7.wireOp",EDGE,"E48.right"),sQuery(id+"F7.wireOp",EDGE,"E49"),sQuery(id+"F7.wireOp",EDGE,"E50"),sQuery(id+"F7.wireOp",EDGE,"E51.filletArc"),sQuery(id+"F7.wireOp",EDGE,"E52.filletArc"),sQuery(id+"F7.wireOp",EDGE,"E53.filletArc"),sQuery(id+"F7.wireOp",EDGE,"E54.filletArc"),sQuery(id+"F7.wireOp",EDGE,"E56.left"),sQuery(id+"F7.wireOp",EDGE,"E56.right")])]});
            transform(context, id + "F14", {"entities" : qUnion([Q0]), "transformType" : TransformType.TRANSLATION_3D, "dx" : 28 * mm, "dy" : 0 * mm, "dz" : 0 * mm, "makeCopy" : true});
        }
    });
